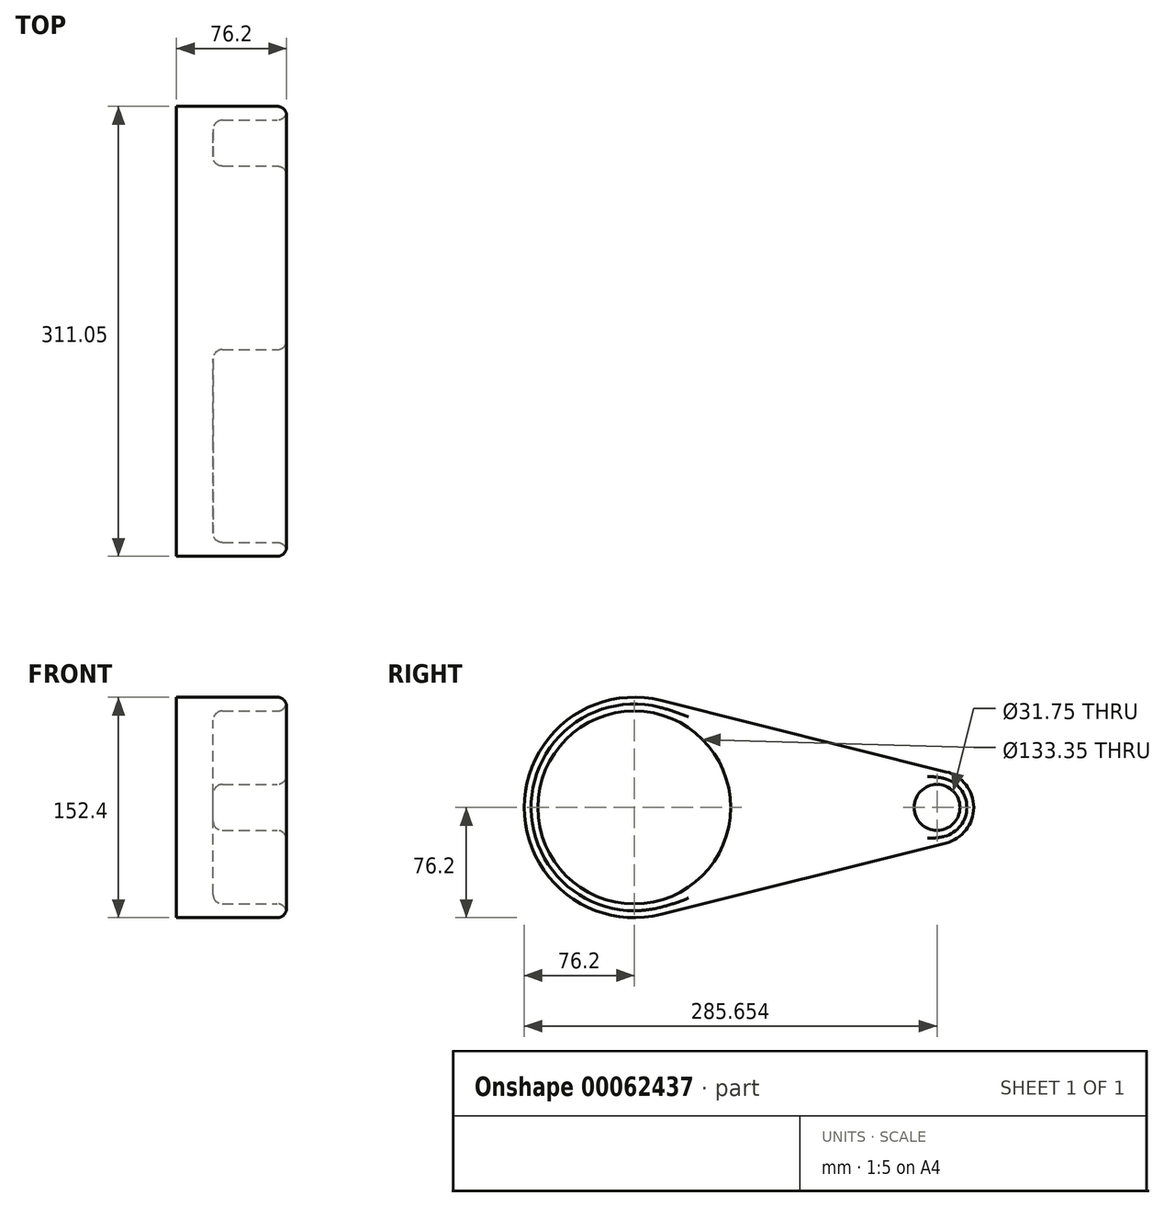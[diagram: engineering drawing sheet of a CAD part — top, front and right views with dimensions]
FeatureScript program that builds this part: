
annotation { "Feature Type Name" : "Feature", "Feature Type Description" : "" }
export const myFeature = defineFeature(function(context is Context, id is Id, definition is map)
    precondition{}
    {
        {
            var Q0;
            Q0=qCreatedBy(makeId("Right.planeOp"),FACE);
            var sketch = newSketch(context, id + "F0", { "sketchPlane" : qUnion([Q0])});
            skCircle(sketch, "E0", {"center": v(0, 0) * mm, "radius": 76.2 * mm});
            skCircle(sketch, "E1", {"center": v(209.45, 0) * mm, "radius": 25.4 * mm});
            skLineSegment(sketch, "E2", {"start": v(18.48, 73.92) * mm, "end": v(215.61, 24.64) * mm});
            skLineSegment(sketch, "E3", {"start": v(18.48, -73.92) * mm, "end": v(215.61, -24.64) * mm});
            skSolve(sketch);
        }
        {
            var Q0;
            {var subQ0=sQuery(id+"F0.wireOp",EDGE,"E0");var subQ1=makeQuery(id+"F0.imprint","INTERSECT",VERTEX,{"derivedFrom":[subQ0,sQuery(id+"F0.wireOp",EDGE,"E2")]});Q0=makeQuery(id+"F0.imprint","IMPRINT",FACE,{"disambiguationData":[TD([[makeQuery(id+"F0.imprint","IMPRINT",EDGE,{"disambiguationData":[TD([[subQ1,-1.0]])],"derivedFrom":subQ0}),1.0]])]});}
            var Q1;
            {var subQ0=sQuery(id+"F0.wireOp",EDGE,"E2");Q1=makeQuery(id+"F0.imprint","IMPRINT",FACE,{"disambiguationData":[TD([[makeQuery(id+"F0.imprint","IMPRINT",EDGE,{"derivedFrom":subQ0}),-1.0]])]});}
            var Q2;
            {var subQ0=sQuery(id+"F0.wireOp",EDGE,"E1");var subQ1=makeQuery(id+"F0.imprint","INTERSECT",VERTEX,{"derivedFrom":[subQ0,sQuery(id+"F0.wireOp",EDGE,"E2")]});Q2=makeQuery(id+"F0.imprint","IMPRINT",FACE,{"disambiguationData":[TD([[makeQuery(id+"F0.imprint","IMPRINT",EDGE,{"disambiguationData":[TD([[subQ1,-1.0]])],"derivedFrom":subQ0}),1.0]])]});}
            extrude(context, id + "F1", {"entities" : qUnion([Q0, Q1, Q2]), "depth" : 76.2 * mm});
        }
        {
            var Q0;
            Q0=makeQuery(id+"F1.opExtrude","CAP_FACE",FACE,{"disambiguationData":[OSD([sQuery(id+"F0.wireOp",EDGE,"E0"),sQuery(id+"F0.wireOp",EDGE,"E1"),sQuery(id+"F0.wireOp",EDGE,"E2"),sQuery(id+"F0.wireOp",EDGE,"E3")])],"isStart":false});
            var sketch = newSketch(context, id + "F2", { "sketchPlane" : qUnion([Q0])});
            skCircle(sketch, "E4", {"center": v(0, 0) * mm, "radius": 66.68 * mm});
            skCircle(sketch, "E5", {"center": v(209.45, 0) * mm, "radius": 15.88 * mm});
            skSolve(sketch);
        }
        {
            var Q0;
            Q0 = qSketchRegion(id + "F2", true);
            extrude(context, id + "F3", {"entities" : qUnion([Q0]), "operationType" : NewBodyOperationType.REMOVE, "oppositeDirection" : true, "depth" : 50.8 * mm});
        }
        {
            var Q0;
            Q0=makeQuery(id+"F1.opExtrude","CAP_FACE",FACE,{"disambiguationData":[OSD([sQuery(id+"F0.wireOp",EDGE,"E0"),sQuery(id+"F0.wireOp",EDGE,"E1"),sQuery(id+"F0.wireOp",EDGE,"E2"),sQuery(id+"F0.wireOp",EDGE,"E3")])],"isStart":false});
            var Q1;
            Q1=makeQuery(id+"F3.boolean.opBoolean","COPY",EDGE,{"derivedFrom":makeQuery(id+"F3.opExtrude","CAP_EDGE",EDGE,{"disambiguationData":[OSD([sQuery(id+"F2.wireOp",EDGE,"E5")])],"isStart":false})});
            var Q2;
            Q2=makeQuery(id+"F3.boolean.opBoolean","COPY",EDGE,{"derivedFrom":makeQuery(id+"F3.opExtrude","CAP_EDGE",EDGE,{"disambiguationData":[OSD([sQuery(id+"F2.wireOp",EDGE,"E4")])],"isStart":false})});
            fillet(context, id + "F4", {"entities" : qUnion([Q0, Q1, Q2]), "radius" : 6.35 * mm, "tangentPropagation" : true, "allowEdgeOverflow" : false});
        }
    });
